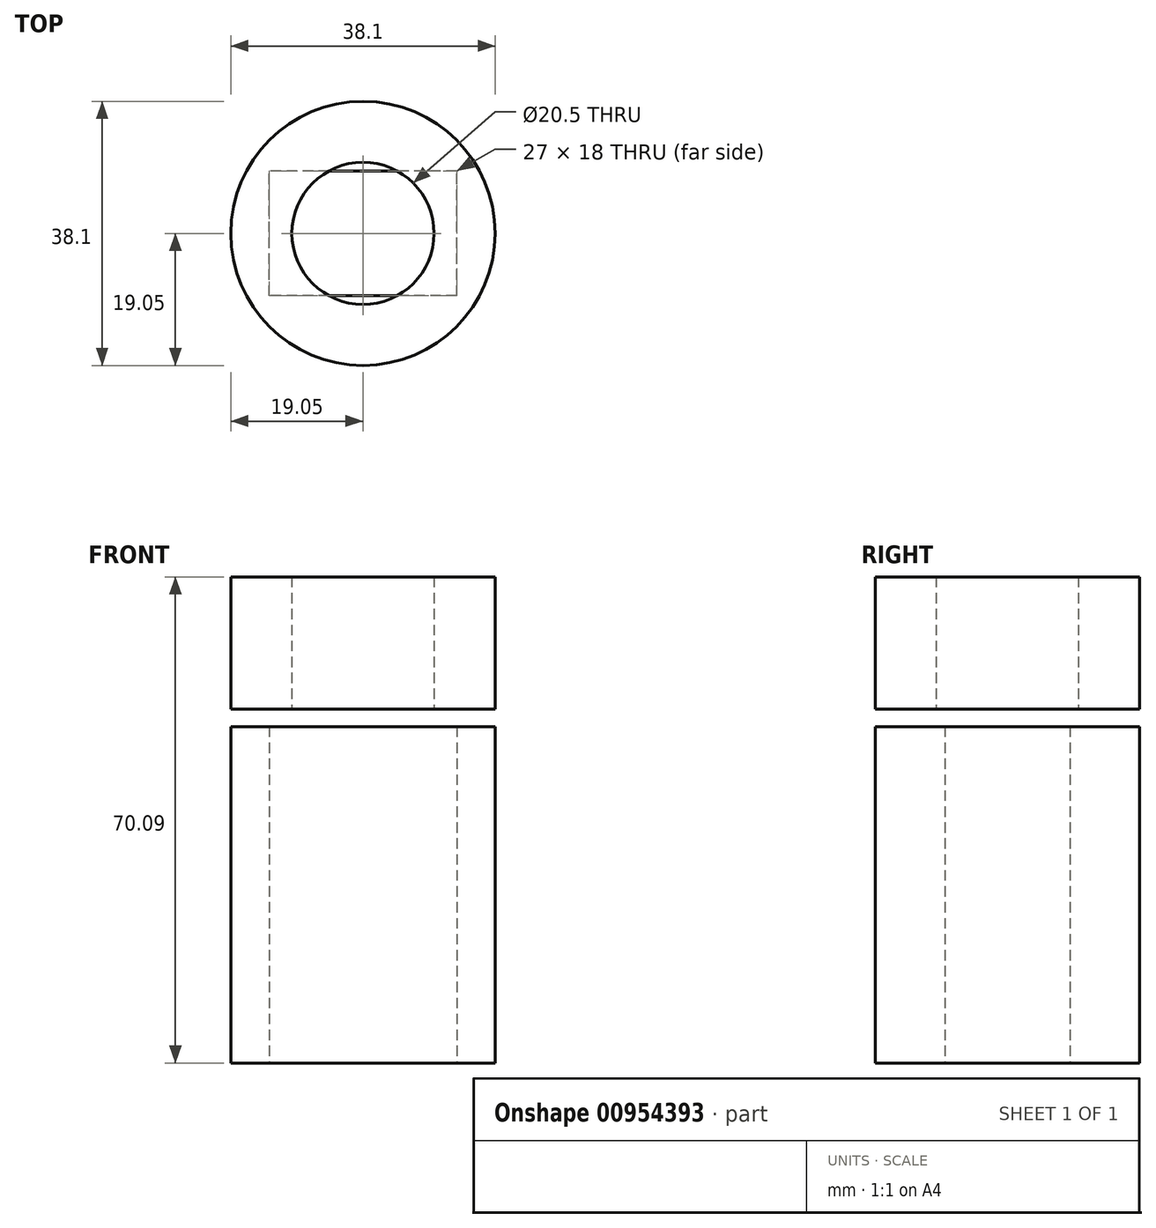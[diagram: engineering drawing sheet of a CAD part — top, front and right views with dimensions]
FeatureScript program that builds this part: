
annotation { "Feature Type Name" : "Feature", "Feature Type Description" : "" }
export const myFeature = defineFeature(function(context is Context, id is Id, definition is map)
    precondition{}
    {
        {
            var Q0;
            Q0=qCreatedBy(makeId("Top.planeOp"),FACE);
            var sketch = newSketch(context, id + "F0", { "sketchPlane" : qUnion([Q0])});
            skLineSegment(sketch, "E0.bottom", {"start": v(13.5, -9) * mm, "end": v(-13.5, -9) * mm});
            skLineSegment(sketch, "E0.top", {"start": v(13.5, 9) * mm, "end": v(-13.5, 9) * mm});
            skLineSegment(sketch, "E0.left", {"start": v(13.5, -9) * mm, "end": v(13.5, 9) * mm});
            skLineSegment(sketch, "E0.right", {"start": v(-13.5, -9) * mm, "end": v(-13.5, 9) * mm});
            skPoint(sketch, "E0.middle", {"position": v(0, 0) * mm});
            skCircle(sketch, "E1", {"center": v(0, 0) * mm, "radius": 19.05 * mm});
            skSolve(sketch);
        }
        {
            var Q0;
            Q0 = qSketchRegion(id + "F0", true);
            extrude(context, id + "F1", {"entities" : qUnion([Q0]), "depth" : 48.5 * mm, "offsetDistance" : 25.4 * mm});
        }
        {
            var Q0;
            Q0=makeQuery(id+"F1.opExtrude","CAP_FACE",FACE,{"disambiguationData":[OSD([sQuery(id+"F0.wireOp",EDGE,"E0.bottom"),sQuery(id+"F0.wireOp",EDGE,"E0.top"),sQuery(id+"F0.wireOp",EDGE,"E0.left"),sQuery(id+"F0.wireOp",EDGE,"E0.right"),sQuery(id+"F0.wireOp",EDGE,"E1")])],"isStart":false});
            cPlane(context, id + "F2", {"entities" : qUnion([Q0]), "cplaneType" : CPlaneType.OFFSET, "offset" : 2.54 * mm, "width" : 152.4 * mm, "height" : 152.4 * mm});
        }
        {
            var Q0;
            Q0=qCreatedBy(id+"F2.planeOp",FACE);
            var sketch = newSketch(context, id + "F3", { "sketchPlane" : qUnion([Q0])});
            skCircle(sketch, "E2", {"center": v(0, 0) * mm, "radius": 10.25 * mm});
            skCircle(sketch, "E3", {"center": v(0, 0) * mm, "radius": 19.05 * mm});
            skSolve(sketch);
        }
        {
            var Q0;
            Q0 = qSketchRegion(id + "F3", true);
            extrude(context, id + "F4", {"entities" : qUnion([Q0]), "depth" : 19.05 * mm, "offsetDistance" : 25.4 * mm});
        }
    });
